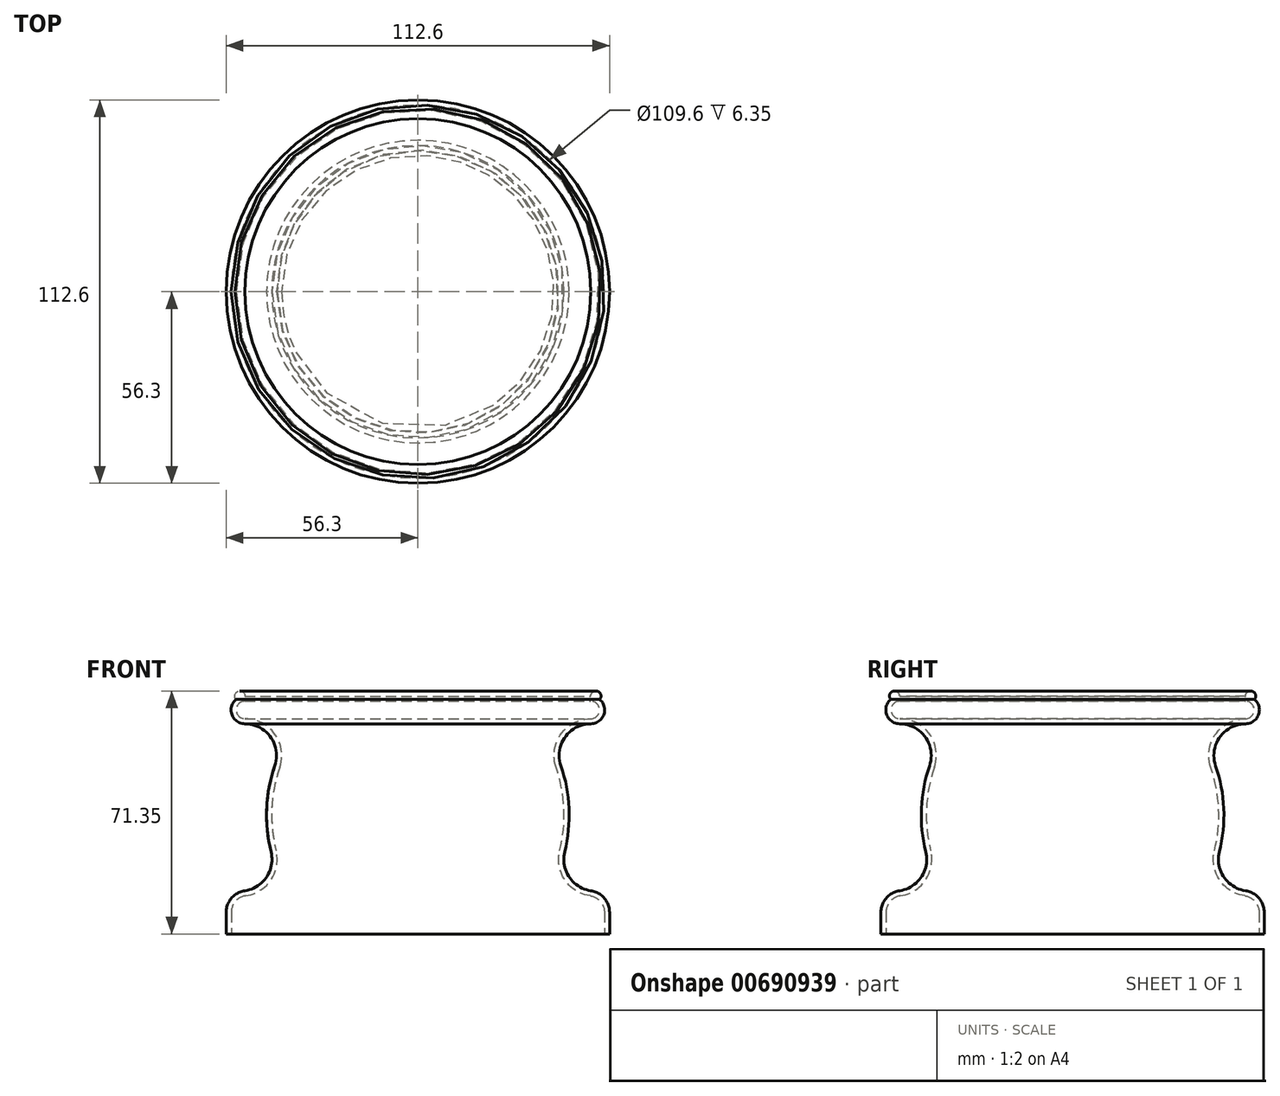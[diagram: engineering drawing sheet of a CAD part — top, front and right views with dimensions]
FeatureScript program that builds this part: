
annotation { "Feature Type Name" : "Feature", "Feature Type Description" : "" }
export const myFeature = defineFeature(function(context is Context, id is Id, definition is map)
    precondition{}
    {
        {
            var Q0;
            Q0=qCreatedBy(makeId("Front.planeOp"),FACE);
            var sketch = newSketch(context, id + "F0", { "sketchPlane" : qUnion([Q0])});
            skLineSegment(sketch, "E0", {"start": v(0, 0) * mm, "end": v(56.3, 0) * mm});
            skLineSegment(sketch, "E1", {"start": v(50.8, 0) * mm, "end": v(50.8, 12.7) * mm, "construction": true});
            skLineSegment(sketch, "E2", {"start": v(0, 0) * mm, "end": v(0, 69.85) * mm});
            skArc(sketch, "E3", {"start": v(56.3, 6.35) * mm, "mid": v(54.73, 10.55) * mm, "end": v(50.8, 12.7) * mm});
            skLineSegment(sketch, "E4", {"start": v(0, 69.85) * mm, "end": v(50.8, 69.85) * mm});
            skArc(sketch, "E5", {"start": v(50.8, 61.72) * mm, "mid": v(54.86, 65.79) * mm, "end": v(50.8, 69.85) * mm});
            skArc(sketch, "E6", {"start": v(43.12, 24.14) * mm, "mid": v(44.4, 36.86) * mm, "end": v(42.02, 49.41) * mm});
            skPoint(sketch, "E7.newPointA", {"position": v(0, 60.32) * mm});
            skArc(sketch, "E7.filletArc", {"start": v(50.8, 61.72) * mm, "mid": v(43.24, 57.83) * mm, "end": v(42.02, 49.41) * mm});
            skArc(sketch, "E8.filletArc", {"start": v(43.12, 24.14) * mm, "mid": v(44.42, 16.71) * mm, "end": v(50.8, 12.7) * mm});
            skLineSegment(sketch, "E9", {"start": v(56.3, 6.35) * mm, "end": v(56.3, 0) * mm});
            skSolve(sketch);
        }
        {
            var Q0;
            Q0 = qSketchRegion(id + "F0", true);
            var Q1;
            Q1=sQuery(id+"F0.wireOp",EDGE,"E2");
            revolve(context, id + "F1", {"entities" : qUnion([Q0]), "axis" : qUnion([Q1]), "revolveType" : RevolveType.FULL});
        }
        {
            var Q0;
            Q0=makeQuery(id+"F1.opRevolve","SWEPT_FACE",FACE,{"disambiguationData":[OSD([sQuery(id+"F0.wireOp",EDGE,"E0")])]});
            shell(context, id + "F2", {"entities" : qUnion([Q0]), "thickness" : 1.5 * mm});
        }
        {
            var Q0;
            Q0=qCreatedBy(makeId("Front.planeOp"),FACE);
            var sketch = newSketch(context, id + "F3", { "sketchPlane" : qUnion([Q0])});
            skLineSegment(sketch, "E10.0", {"start": v(50.8, 69.85) * mm, "end": v(-50.8, 69.85) * mm, "construction": true});
            skCircle(sketch, "E11", {"center": v(52.3, 69.85) * mm, "radius": 1.5 * mm});
            skLineSegment(sketch, "E12", {"start": v(0, 69.85) * mm, "end": v(0, 0) * mm, "construction": true});
            skSolve(sketch);
        }
        {
            var Q0;
            Q0 = qSketchRegion(id + "F3", true);
            var Q1;
            Q1=sQuery(id+"F3.wireOp",EDGE,"E12");
            revolve(context, id + "F4", {"operationType" : NewBodyOperationType.ADD, "entities" : qUnion([Q0]), "axis" : qUnion([Q1]), "revolveType" : RevolveType.FULL});
        }
    });
